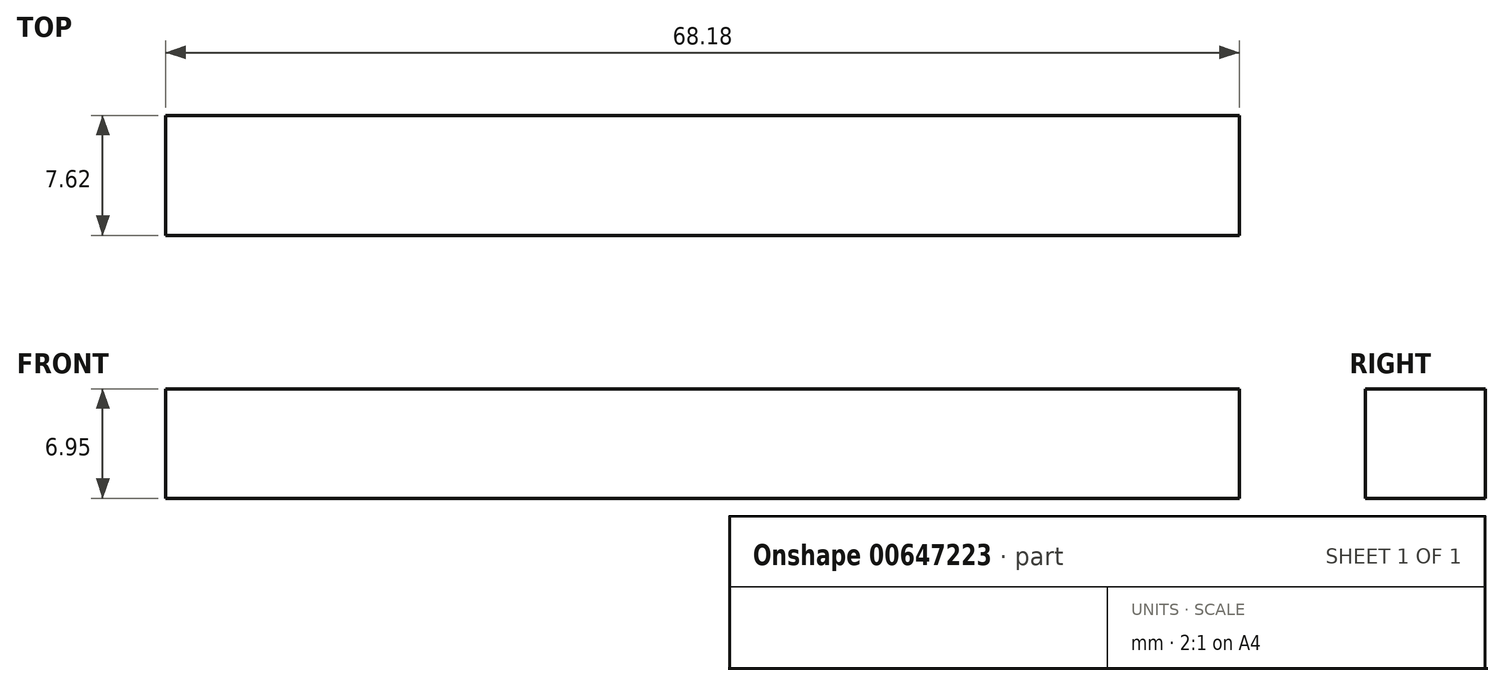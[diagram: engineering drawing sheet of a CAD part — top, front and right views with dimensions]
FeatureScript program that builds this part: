
annotation { "Feature Type Name" : "Feature", "Feature Type Description" : "" }
export const myFeature = defineFeature(function(context is Context, id is Id, definition is map)
    precondition{}
    {
        {
            var Q0;
            Q0=qCreatedBy(makeId("Front.planeOp"),FACE);
            var sketch = newSketch(context, id + "F0", { "sketchPlane" : qUnion([Q0])});
            skLineSegment(sketch, "E0.bottom", {"start": v(-35.07, 0) * mm, "end": v(33.11, 0) * mm});
            skLineSegment(sketch, "E0.top", {"start": v(-35.07, 6.95) * mm, "end": v(33.11, 6.95) * mm});
            skLineSegment(sketch, "E0.left", {"start": v(-35.07, 0) * mm, "end": v(-35.07, 6.95) * mm});
            skLineSegment(sketch, "E0.right", {"start": v(33.11, 0) * mm, "end": v(33.11, 6.95) * mm});
            skLineSegment(sketch, "E1.bottom", {"start": v(-3.8, 6.95) * mm, "end": v(3.37, 6.95) * mm});
            skLineSegment(sketch, "E1.top", {"start": v(-3.8, 73.39) * mm, "end": v(3.37, 73.39) * mm});
            skLineSegment(sketch, "E1.left", {"start": v(-3.8, 6.95) * mm, "end": v(-3.8, 73.39) * mm});
            skLineSegment(sketch, "E1.right", {"start": v(3.37, 6.95) * mm, "end": v(3.37, 73.39) * mm});
            skSolve(sketch);
        }
        {
            var Q0;
            Q0=makeQuery(id+"F0.imprint","IMPRINT",FACE,{"disambiguationData":[TD([[makeQuery(id+"F0.imprint","IMPRINT",EDGE,{"derivedFrom":sQuery(id+"F0.wireOp",EDGE,"E0.bottom")}),1.0]])]});
            var Q1;
            Q1=makeQuery(id+"F0.imprint","IMPRINT",FACE,{"disambiguationData":[TD([[makeQuery(id+"F0.imprint","IMPRINT",EDGE,{"derivedFrom":sQuery(id+"F0.wireOp",EDGE,"E1.bottom")}),1.0]])]});
            extrude(context, id + "F1", {"entities" : qUnion([Q0, Q1]), "depth" : 7.62 * mm, "offsetDistance" : 25.4 * mm});
        }
    });
